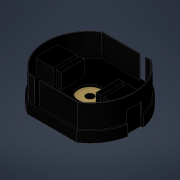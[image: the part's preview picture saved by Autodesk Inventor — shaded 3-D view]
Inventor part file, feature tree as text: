
AUTODESK INVENTOR PART (.ipt)
format: ipt  version: 2021 (Build 250183000, 183)  size: 347,648 bytes
history: native  units: mm
features: other x21, extrude x15, sketch x13, imported_body x1
ambient origin geometry x8: Origin, YZ Plane, XZ Plane, XY Plane, X Axis, Y Axis, Z Axis, Center Point
bodies: Body1 (feature_tree)
feature tree (50):
  imported_body  "Base"
  other  "Sólido1"
  extrude  "Extrusão1"  Depth=1.3mm
  sketch  "Esboço13"  dims[d46=3.0mm d47=0.0mm d48=0.7mm]
  extrude  "Extrusão13"  Depth=0.7mm
  extrude  "Extrusão14"  Depth=0.7mm
  extrude  "Extrusão15"  Depth=3.0mm TaperAngle=0.0deg
  other  "Plano de trabalho3"
  sketch  "Esboço15"  dims[d51=0.7mm d52=3.0mm d53=0.0mm]
  other  "Plano de trabalho4"
  sketch  "Esboço16"  dims[d54=1.0mm d55=0.0mm d56=2.0mm]
  other  "Plano de trabalho5"
  extrude  "Extrusão16"  Depth=2.0mm
  other  "Plano de trabalho6"
  extrude  "Extrusão17"  Depth=3.0mm
  sketch  "Esboço20"  dims[d68=3.0mm d69=0.4mm]
  extrude  "Extrusão18"  Depth=3.537mm TaperAngle=0.0deg
  extrude  "Extrusão19"  Depth=0.4mm
  sketch  "Esboço21"  dims[d70=3.1mm d71=0.1mm]
  extrude  "Extrusão20"  Depth=0.1mm
  extrude  "Extrusão21"  Depth=3.4mm TaperAngle=0.0deg
  extrude  "Extrusão22"  Depth=0.3mm TaperAngle=0.0deg
  extrude  "Extrusão23"  Depth=1.0mm TaperAngle=0.0deg
  other  "Plano de trabalho7"
  other  "Plano de trabalho8"
  extrude  "Extrusão24"  Depth=0.5mm
  extrude  "Extrusão25"  Depth=0.8mm TaperAngle=0.0deg
  other  "Ponto de trabalho1"
  other  "Eixo de trabalho1"
  other  "Eixo de trabalho2"
  other  "Ponto de trabalho3"
  other  "Ponto de trabalho4"
  other  "Eixo de trabalho3"
  extrude  "Extrusão26"  Depth=2.9mm
  sketch  "Esboço1"  dims[d0=1.4mm d1=0.0mm d45=1.3mm]
  sketch  "Esboço14"  dims[d49=0.7mm d50=0.7mm]
  sketch  "Esboço17"  dims[d57=2.0mm d58=3.0mm]
  sketch  "Esboço18"  dims[d59=3.537mm d60=0.0mm d61=3.537mm d62=0.0mm]
  other  "Contorno projetado6"
  sketch  "Esboço22"  dims[d72=2.0mm d73=0.0mm d74=3.4mm d75=0.0mm]
  other  "Contorno projetado7"
  other  "Contorno projetado8"
  other  "Contorno projetado9"
  other  "Contorno projetado10"
  sketch  "Esboço23"  dims[d76=3.0mm d77=0.3mm d78=0.0mm]
  sketch  "Esboço24"  dims[d79=1.0mm d80=1.55mm d81=0.0mm]
  sketch  "Esboço25"  dims[d82=2.0mm d83=0.0mm d84=5.0mm d85=0.8mm d86=0.0mm d87=2.9mm d88=2.0mm d89=2.9mm d90=0.4mm d91=0.0mm d92=0.4mm d93=0.0mm d97=45.0deg d101=2.0mm d102=2.0mm d103=0.0mm d26=1.0mm d27=1.0mm d28=1.0mm d29=0.15mm d30=0.25mm d31=0.375mm d32=14.3117mm d33=0.75mm d34=20.594885mm d35=0.0625mm d36=0.75mm d37=0.375mm d94=0.5mm d95=0.872665mm]
  other  "Contorno projetado11"
  other  "Ponto de trabalho2"
  other  "Ponto de trabalho5"
